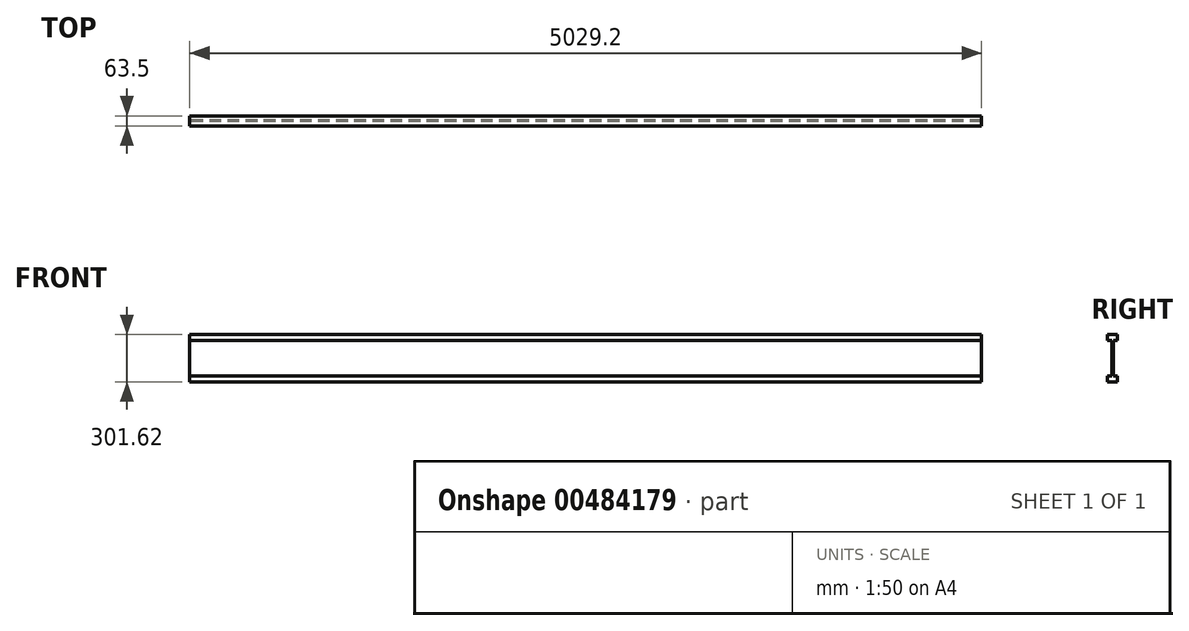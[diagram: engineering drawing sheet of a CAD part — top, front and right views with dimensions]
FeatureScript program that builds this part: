
annotation { "Feature Type Name" : "Feature", "Feature Type Description" : "" }
export const myFeature = defineFeature(function(context is Context, id is Id, definition is map)
    precondition{}
    {
        {
            var Q0;
            Q0=qCreatedBy(makeId("Right.planeOp"),FACE);
            var sketch = newSketch(context, id + "F0", { "sketchPlane" : qUnion([Q0])});
            skLineSegment(sketch, "E0", {"start": v(0, 0) * mm, "end": v(63.5, 0) * mm});
            skLineSegment(sketch, "E1", {"start": v(63.5, 0) * mm, "end": v(63.5, 38.1) * mm});
            skLineSegment(sketch, "E2", {"start": v(63.5, 38.1) * mm, "end": v(36.51, 38.1) * mm});
            skLineSegment(sketch, "E3", {"start": v(36.51, 38.1) * mm, "end": v(36.51, 263.53) * mm});
            skLineSegment(sketch, "E4", {"start": v(36.51, 263.53) * mm, "end": v(63.5, 263.53) * mm});
            skLineSegment(sketch, "E5", {"start": v(63.5, 263.53) * mm, "end": v(63.5, 301.63) * mm});
            skLineSegment(sketch, "E6", {"start": v(63.5, 301.63) * mm, "end": v(0, 301.63) * mm});
            skLineSegment(sketch, "E7", {"start": v(0, 301.63) * mm, "end": v(0, 263.53) * mm});
            skLineSegment(sketch, "E8", {"start": v(0, 263.53) * mm, "end": v(26.99, 263.53) * mm});
            skLineSegment(sketch, "E9", {"start": v(26.99, 263.53) * mm, "end": v(26.99, 38.1) * mm});
            skLineSegment(sketch, "E10", {"start": v(26.99, 38.1) * mm, "end": v(0, 38.1) * mm});
            skLineSegment(sketch, "E11", {"start": v(0, 38.1) * mm, "end": v(0, 0) * mm});
            skSolve(sketch);
        }
        {
            var Q0;
            Q0 = qSketchRegion(id + "F0", true);
            extrude(context, id + "F1", {"entities" : qUnion([Q0]), "depth" : 5029.2 * mm});
        }
    });
